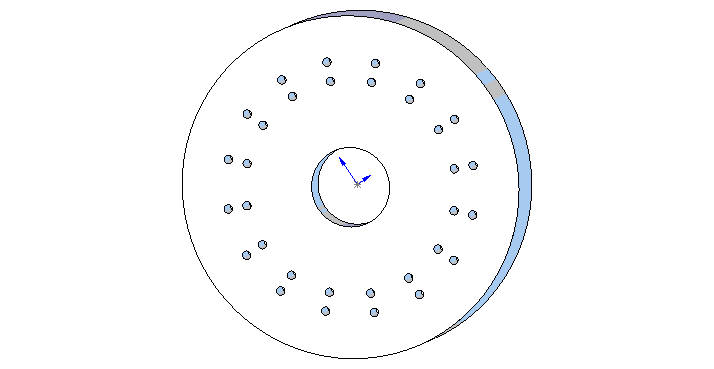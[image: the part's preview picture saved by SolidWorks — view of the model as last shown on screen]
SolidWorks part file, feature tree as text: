
SOLIDWORKS PART (.sldprt)
format: sldprt  version: not decoded by parser v0  size: 276,992 bytes
history: native  units: mm
features: sketch x4, extrude x2, cut_extrude x2 (+11 scaffold rows collapsed)
feature tree (19):
  scaffold x11  (default folders/planes/origin — collapsed)
  sketch  "Sketch1"  dims[D1=23.75mm]
  extrude  "Extrude1"  Depth=5mm
  sketch  "Sketch4"  dims[D1=~1.149337mm]
  sketch  "Sketch5"  dims[D1=27.0mm]
  extrude  "Extrude3"  Depth=5mm
  sketch  "Sketch6"  dims[D1=10.0mm]
  cut_extrude  "Cut-Extrude4"  Depth=5mm
  cut_extrude  "Cut-Extrude5"  Depth=5mm
decode coverage: 8 of 8 modeling features carry decoded parameters
note: ~ marks probable driven/reference dimensions
note: suppression state not decoded; provenance and decode notes live in map.json
